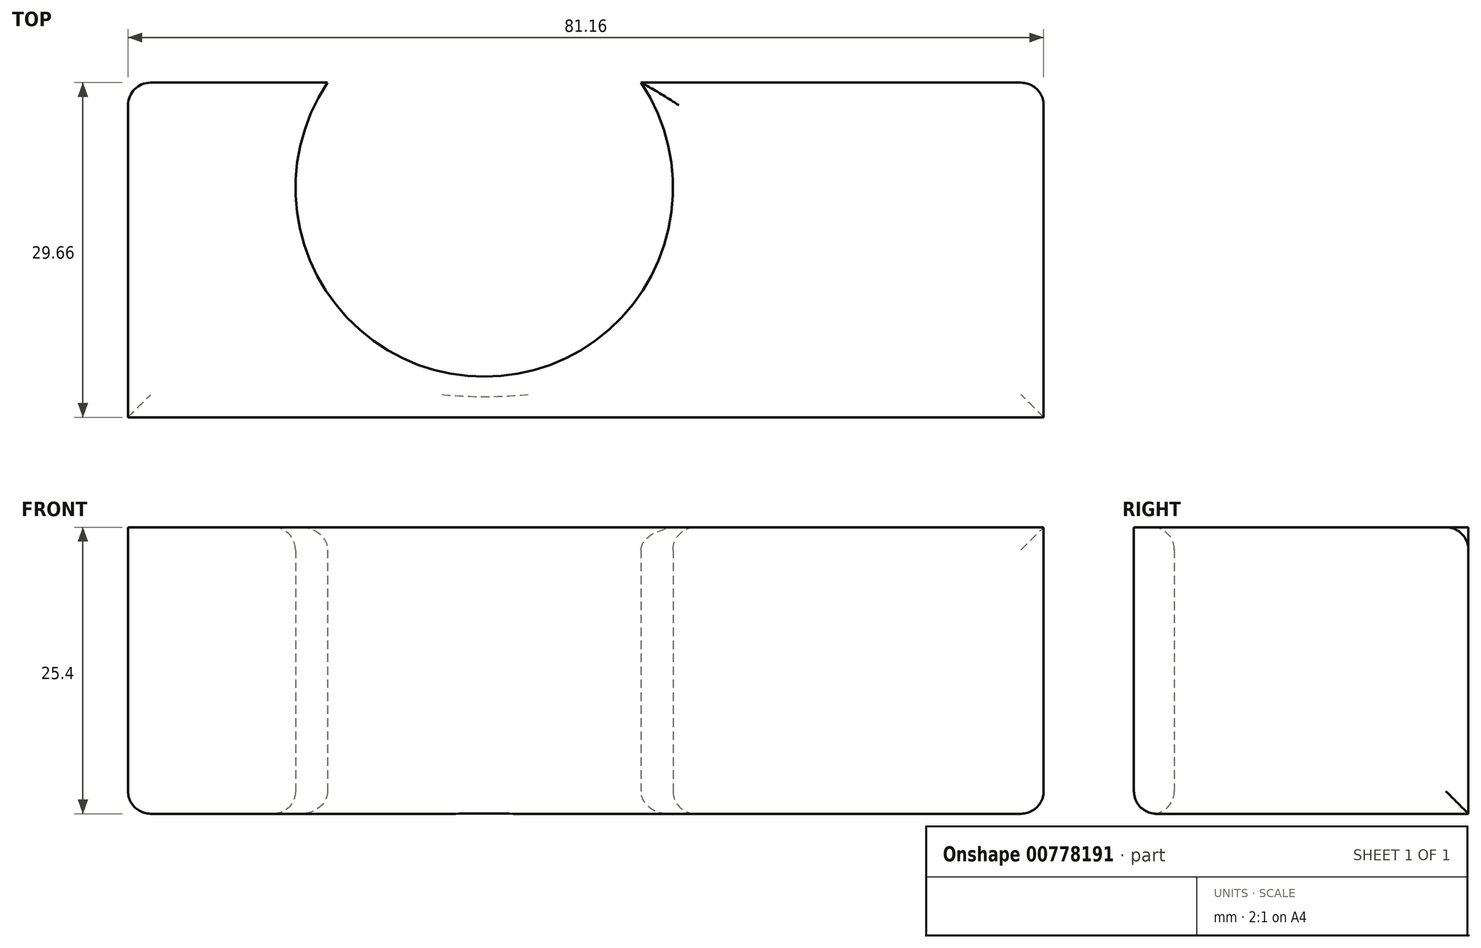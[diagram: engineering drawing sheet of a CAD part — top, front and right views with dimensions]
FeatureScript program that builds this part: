
annotation { "Feature Type Name" : "Feature", "Feature Type Description" : "" }
export const myFeature = defineFeature(function(context is Context, id is Id, definition is map)
    precondition{}
    {
        {
            var Q0;
            Q0=qCreatedBy(makeId("Top.planeOp"),FACE);
            var sketch = newSketch(context, id + "F0", { "sketchPlane" : qUnion([Q0])});
            skLineSegment(sketch, "E0.bottom", {"start": v(-31.58, 0) * mm, "end": v(49.58, 0) * mm});
            skLineSegment(sketch, "E0.top", {"start": v(-31.58, -29.66) * mm, "end": v(49.58, -29.66) * mm});
            skLineSegment(sketch, "E0.left", {"start": v(-31.58, 0) * mm, "end": v(-31.58, -29.66) * mm});
            skLineSegment(sketch, "E0.right", {"start": v(49.58, 0) * mm, "end": v(49.58, -29.66) * mm});
            skCircle(sketch, "E1", {"center": v(0, -9.33) * mm, "radius": 16.73 * mm});
            skLineSegment(sketch, "E2", {"start": v(0, 41.9) * mm, "end": v(0, -82.03) * mm});
            skSolve(sketch);
        }
        {
            var Q0;
            {var subQ5=sQuery(id+"F0.wireOp",EDGE,"E0.right");Q0=makeQuery(id+"F0.imprint","IMPRINT",FACE,{"disambiguationData":[TD([[makeQuery(id+"F0.imprint","IMPRINT",EDGE,{"derivedFrom":subQ5}),-1.0]])]});}
            var Q1;
            {var subQ0=sQuery(id+"F0.wireOp",EDGE,"E0.left");Q1=makeQuery(id+"F0.imprint","IMPRINT",FACE,{"disambiguationData":[TD([[makeQuery(id+"F0.imprint","IMPRINT",EDGE,{"derivedFrom":subQ0}),1.0]])]});}
            var Q2;
            {var subQ0=sQuery(id+"F0.wireOp",EDGE,"E1");var subQ1=sQuery(id+"F0.wireOp",EDGE,"E0.bottom");var subQ2=makeQuery(id+"F0.imprint","INTERSECT",VERTEX,{"disambiguationData":[OD(0.0)],"derivedFrom":[subQ1,subQ0]});Q2=makeQuery(id+"F0.imprint","IMPRINT",FACE,{"disambiguationData":[TD([[makeQuery(id+"F0.imprint","IMPRINT",EDGE,{"disambiguationData":[TD([[subQ2,-1.0]])],"derivedFrom":subQ1}),1.0]])]});}
            var Q3;
            {var subQ0=sQuery(id+"F0.wireOp",EDGE,"E1");var subQ1=sQuery(id+"F0.wireOp",EDGE,"E0.bottom");var subQ2=makeQuery(id+"F0.imprint","INTERSECT",VERTEX,{"disambiguationData":[OD(1.0)],"derivedFrom":[subQ1,subQ0]});Q3=makeQuery(id+"F0.imprint","IMPRINT",FACE,{"disambiguationData":[TD([[makeQuery(id+"F0.imprint","IMPRINT",EDGE,{"disambiguationData":[TD([[subQ2,1.0]])],"derivedFrom":subQ1}),1.0]])]});}
            extrude(context, id + "F1", {"entities" : qUnion([Q0, Q1, Q2, Q3]), "depth" : 25.4 * mm, "offsetDistance" : 25.4 * mm});
        }
        {
            var Q0;
            Q0=makeQuery(id+"F1.opExtrude","CAP_EDGE",EDGE,{"disambiguationData":[OSD([sQuery(id+"F0.wireOp",EDGE,"E0.top")])],"isStart":true});
            var Q1;
            Q1=makeQuery(id+"F1.opExtrude","CAP_EDGE",EDGE,{"disambiguationData":[OSD([sQuery(id+"F0.wireOp",EDGE,"E0.left")])],"isStart":true});
            var Q2;
            Q2=makeQuery(id+"F1.opExtrude","CAP_EDGE",EDGE,{"disambiguationData":[OSD([sQuery(id+"F0.wireOp",EDGE,"E0.right")])],"isStart":true});
            var Q3;
            {var subQ0=sQuery(id+"F0.wireOp",EDGE,"E1");var subQ1=makeQuery(id+"F0.imprint","INTERSECT",VERTEX,{"disambiguationData":[OD(0.0)],"derivedFrom":[subQ0,sQuery(id+"F0.wireOp",EDGE,"E2")]});Q3=makeQuery(id+"F1.opExtrude","CAP_EDGE",EDGE,{"disambiguationData":[OSD([subQ0]),TDD([makeQuery(id+"F0.imprint","IMPRINT",EDGE,{"disambiguationData":[TD([[subQ1,1.0]])],"derivedFrom":subQ0}),makeQuery(id+"F0.imprint","IMPRINT",EDGE,{"disambiguationData":[TD([[subQ1,-1.0]])],"derivedFrom":subQ0})])],"isStart":true});}
            var Q4;
            {var subQ0=sQuery(id+"F0.wireOp",EDGE,"E1");var subQ1=sQuery(id+"F0.wireOp",EDGE,"E0.bottom");Q4=makeQuery(id+"F1.opExtrude","CAP_EDGE",EDGE,{"disambiguationData":[OSD([subQ0]),TDD([makeQuery(id+"F0.imprint","IMPRINT",EDGE,{"disambiguationData":[TD([[makeQuery(id+"F0.imprint","INTERSECT",VERTEX,{"disambiguationData":[OD(0.0)],"derivedFrom":[subQ1,subQ0]}),-1.0]])],"derivedFrom":subQ0}),makeQuery(id+"F0.imprint","IMPRINT",EDGE,{"disambiguationData":[TD([[makeQuery(id+"F0.imprint","INTERSECT",VERTEX,{"disambiguationData":[OD(1.0)],"derivedFrom":[subQ1,subQ0]}),1.0]])],"derivedFrom":subQ0})])],"isStart":true});}
            var Q5;
            {var subQ0=sQuery(id+"F0.wireOp",EDGE,"E1");var subQ1=makeQuery(id+"F0.imprint","INTERSECT",VERTEX,{"disambiguationData":[OD(0.0)],"derivedFrom":[subQ0,sQuery(id+"F0.wireOp",EDGE,"E2")]});Q5=makeQuery(id+"F1.opExtrude","CAP_EDGE",EDGE,{"disambiguationData":[OSD([subQ0]),TDD([makeQuery(id+"F0.imprint","IMPRINT",EDGE,{"disambiguationData":[TD([[subQ1,1.0]])],"derivedFrom":subQ0}),makeQuery(id+"F0.imprint","IMPRINT",EDGE,{"disambiguationData":[TD([[subQ1,-1.0]])],"derivedFrom":subQ0})])],"isStart":false});}
            var Q6;
            {var subQ0=sQuery(id+"F0.wireOp",EDGE,"E0.bottom");Q6=makeQuery(id+"F1.opExtrude","CAP_EDGE",EDGE,{"disambiguationData":[OSD([subQ0]),TDD([makeQuery(id+"F0.imprint","IMPRINT",EDGE,{"disambiguationData":[TD([[makeQuery(id+"F0.imprint","INTERSECT",VERTEX,{"derivedFrom":[subQ0,sQuery(id+"F0.wireOp",EDGE,"E0.right")]}),1.0]])],"derivedFrom":subQ0})])],"isStart":false});}
            var Q7;
            Q7=makeQuery(id+"F1.opExtrude","SWEPT_EDGE",EDGE,{"disambiguationData":[OSD([sQuery(id+"F0.wireOp",EDGE,"E0.bottom"),sQuery(id+"F0.wireOp",EDGE,"E0.right")])]});
            var Q8;
            Q8=makeQuery(id+"F1.opExtrude","SWEPT_EDGE",EDGE,{"disambiguationData":[OSD([sQuery(id+"F0.wireOp",EDGE,"E0.bottom"),sQuery(id+"F0.wireOp",EDGE,"E0.left")])]});
            fillet(context, id + "F2", {"entities" : qUnion([Q0, Q1, Q2, Q3, Q4, Q5, Q6, Q7, Q8]), "radius" : 2 * mm, "tangentPropagation" : true, "allowEdgeOverflow" : false});
        }
    });
